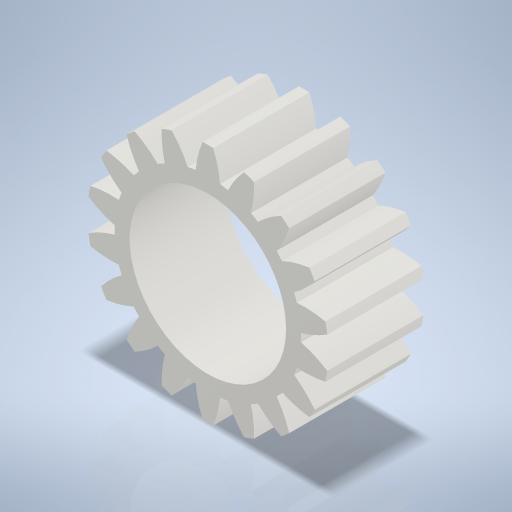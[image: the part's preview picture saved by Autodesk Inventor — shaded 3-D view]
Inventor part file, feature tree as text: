
AUTODESK INVENTOR PART (.ipt)
format: ipt  version: 2024 (Build 280153000, 153)  size: 349,696 bytes
history: native  units: mm (DEFAULTED — no unit token found)
features: plane x3, other x3, sketch x2, extrude x1, hole x1
ambient origin geometry x8: Origin, YZ Plane, XZ Plane, XY Plane, X Axis, Y Axis, Z Axis, Center Point
bodies: Solid1 (feature_tree)
feature tree (10):
  extrude  "Extrusion1"  Depth=8.0mm TaperAngle=0.0deg
  plane  "Work Plane2"
  plane  "Work Plane8"
  plane  "Work Plane9"
  other  "Stirnzahnrad"
  hole  "Bohrung1"  [1 undecoded]
  sketch  "Sketch1"  dims[d0=20.0mm d1=8.0mm d2=0.0mm]
  other  "Srf1"
  sketch  "Skizze3"  dims[d3=18.0mm d4=10.0mm d5=0.0mm d16=18.0mm d17=0.0mm d34=1.745329mm d39=0.0mm d41=0.0mm d43=18.0mm d46=18.0mm d47=0.0mm d48=0.0mm d49=13.0mm d50=6.0mm d51=4.0mm d52=2.0mm d53=90.0deg d54=8.0mm d55=20.594885mm]
  other  "Flankendurchmesser"
note: 1 required parameter value undecoded (feature->parameter linkage not recoverable at this tier; creation-order binding heuristic only, values carry confidence <= 0.55)
